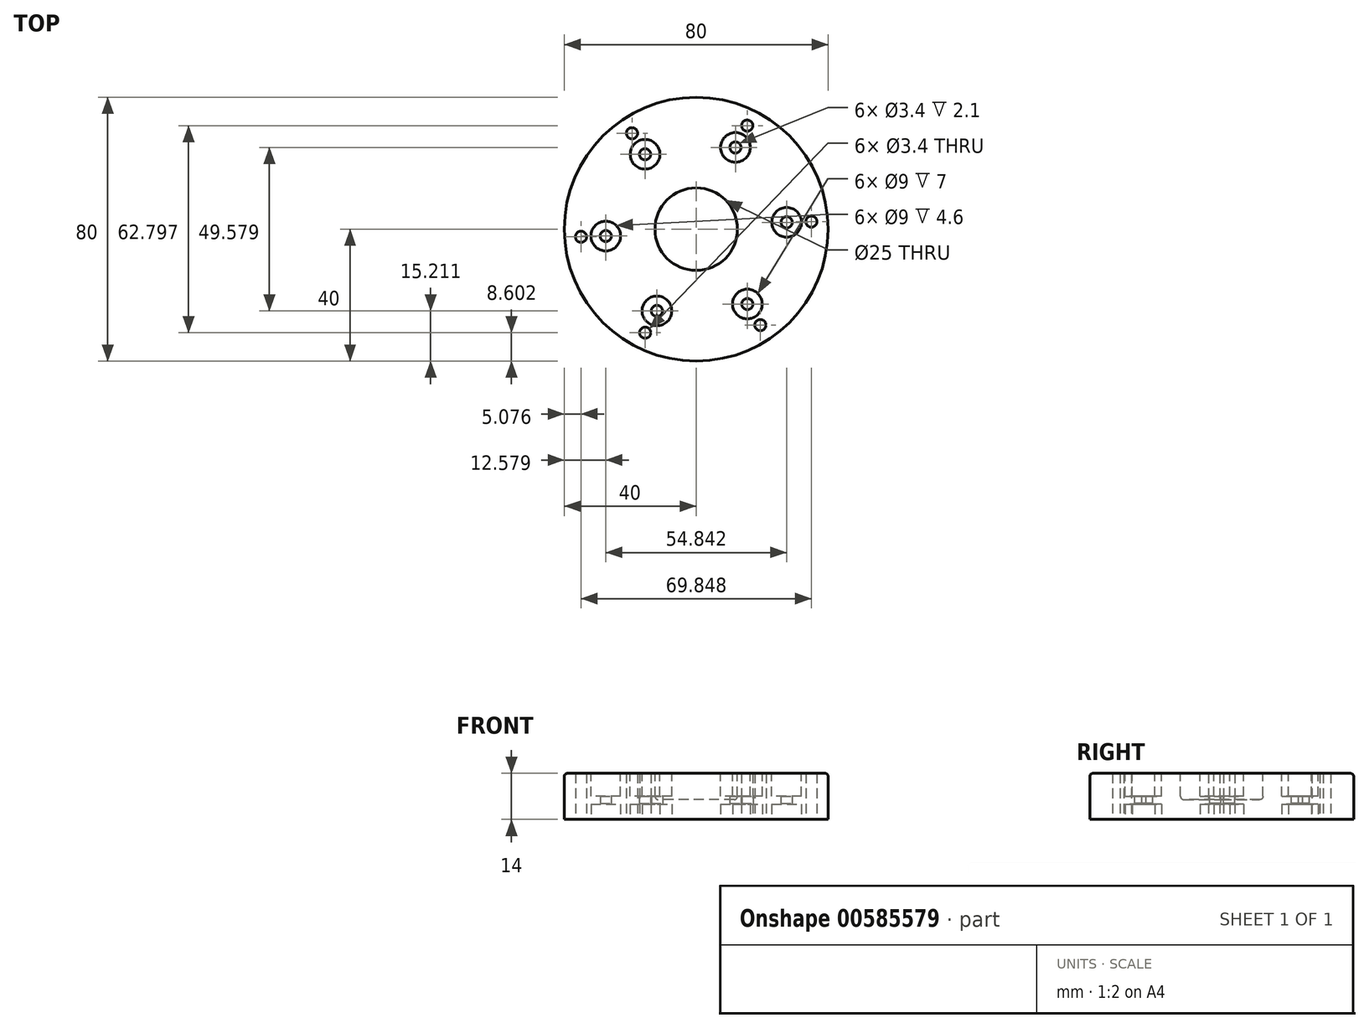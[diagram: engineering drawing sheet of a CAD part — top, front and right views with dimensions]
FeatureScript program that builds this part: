
annotation { "Feature Type Name" : "Feature", "Feature Type Description" : "" }
export const myFeature = defineFeature(function(context is Context, id is Id, definition is map)
    precondition{}
    {
        {
            var Q0;
            Q0=qCreatedBy(makeId("Top.planeOp"),FACE);
            var sketch = newSketch(context, id + "F0", { "sketchPlane" : qUnion([Q0])});
            skCircle(sketch, "E0", {"center": v(0, 0) * mm, "radius": 40 * mm});
            skCircle(sketch, "E1", {"center": v(-19.46, 29.1) * mm, "radius": 1.7 * mm});
            skCircle(sketch, "E2.1.0", {"center": v(15.46, 31.4) * mm, "radius": 1.7 * mm});
            skCircle(sketch, "E2.2.0", {"center": v(34.92, 2.3) * mm, "radius": 1.7 * mm});
            skCircle(sketch, "E2.3.0", {"center": v(19.46, -29.1) * mm, "radius": 1.7 * mm});
            skCircle(sketch, "E2.4.0", {"center": v(-15.46, -31.4) * mm, "radius": 1.7 * mm});
            skCircle(sketch, "E2.5.0", {"center": v(-34.92, -2.3) * mm, "radius": 1.7 * mm});
            skLineSegment(sketch, "E2.anchor1", {"start": v(0, 0) * mm, "end": v(-19.46, 29.1) * mm, "construction": true});
            skLineSegment(sketch, "E2.anchor2", {"start": v(0, 0) * mm, "end": v(-34.92, -2.3) * mm, "construction": true});
            skCircle(sketch, "E3", {"center": v(11.9, 24.79) * mm, "radius": 1.7 * mm});
            skCircle(sketch, "E4.1.0", {"center": v(-15.52, 22.7) * mm, "radius": 1.7 * mm});
            skCircle(sketch, "E4.2.0", {"center": v(-27.42, -2.08) * mm, "radius": 1.7 * mm});
            skCircle(sketch, "E4.3.0", {"center": v(-11.9, -24.79) * mm, "radius": 1.7 * mm});
            skCircle(sketch, "E4.4.0", {"center": v(15.52, -22.7) * mm, "radius": 1.7 * mm});
            skCircle(sketch, "E4.5.0", {"center": v(27.42, 2.08) * mm, "radius": 1.7 * mm});
            skSolve(sketch);
        }
        {
            var Q0;
            Q0=makeQuery(id+"F0.imprint","IMPRINT",FACE,{"disambiguationData":[TD([[makeQuery(id+"F0.imprint","IMPRINT",EDGE,{"derivedFrom":sQuery(id+"F0.wireOp",EDGE,"E1")}),-1.0]])]});
            extrude(context, id + "F1", {"entities" : qUnion([Q0]), "depth" : 14 * mm, "offsetDistance" : 25 * mm});
        }
        {
            var Q0;
            Q0=makeQuery(id+"F1.opExtrude","CAP_FACE",FACE,{"disambiguationData":[OSD([sQuery(id+"F0.wireOp",EDGE,"E1"),sQuery(id+"F0.wireOp",EDGE,"E2.1.0"),sQuery(id+"F0.wireOp",EDGE,"E2.2.0"),sQuery(id+"F0.wireOp",EDGE,"E2.3.0"),sQuery(id+"F0.wireOp",EDGE,"E2.4.0"),sQuery(id+"F0.wireOp",EDGE,"E2.5.0"),sQuery(id+"F0.wireOp",EDGE,"E0"),sQuery(id+"F0.wireOp",EDGE,"E3"),sQuery(id+"F0.wireOp",EDGE,"E4.1.0"),sQuery(id+"F0.wireOp",EDGE,"E4.2.0"),sQuery(id+"F0.wireOp",EDGE,"E4.3.0"),sQuery(id+"F0.wireOp",EDGE,"E4.4.0"),sQuery(id+"F0.wireOp",EDGE,"E4.5.0")])],"isStart":false});
            var sketch = newSketch(context, id + "F2", { "sketchPlane" : qUnion([Q0])});
            skCircle(sketch, "E5.0", {"center": v(-11.9, -24.79) * mm, "radius": 1.7 * mm});
            skCircle(sketch, "E6.0", {"center": v(-27.42, -2.08) * mm, "radius": 1.7 * mm});
            skCircle(sketch, "E7.0", {"center": v(-15.52, 22.7) * mm, "radius": 1.7 * mm});
            skCircle(sketch, "E8.0", {"center": v(11.9, 24.79) * mm, "radius": 1.7 * mm});
            skCircle(sketch, "E9.0", {"center": v(15.52, -22.7) * mm, "radius": 1.7 * mm});
            skCircle(sketch, "E10.0", {"center": v(27.42, 2.08) * mm, "radius": 1.7 * mm});
            skCircle(sketch, "E11", {"center": v(-15.52, 22.7) * mm, "radius": 4.5 * mm});
            skCircle(sketch, "E12.1.0", {"center": v(-27.42, -2.08) * mm, "radius": 4.5 * mm});
            skCircle(sketch, "E12.2.0", {"center": v(-11.9, -24.79) * mm, "radius": 4.5 * mm});
            skCircle(sketch, "E12.3.0", {"center": v(15.52, -22.7) * mm, "radius": 4.5 * mm});
            skCircle(sketch, "E12.4.0", {"center": v(27.42, 2.08) * mm, "radius": 4.5 * mm});
            skCircle(sketch, "E12.5.0", {"center": v(11.9, 24.79) * mm, "radius": 4.5 * mm});
            skPoint(sketch, "E12.center", {"position": v(0, 0) * mm});
            skSolve(sketch);
        }
        {
            var Q0;
            Q0 = qSketchRegion(id + "F2", true);
            extrude(context, id + "F3", {"entities" : qUnion([Q0]), "operationType" : NewBodyOperationType.REMOVE, "oppositeDirection" : true, "depth" : 7 * mm, "offsetDistance" : 25 * mm});
        }
        {
            var Q0;
            Q0=makeQuery(id+"F1.opExtrude","CAP_FACE",FACE,{"disambiguationData":[OSD([sQuery(id+"F0.wireOp",EDGE,"E1"),sQuery(id+"F0.wireOp",EDGE,"E2.1.0"),sQuery(id+"F0.wireOp",EDGE,"E2.2.0"),sQuery(id+"F0.wireOp",EDGE,"E2.3.0"),sQuery(id+"F0.wireOp",EDGE,"E2.4.0"),sQuery(id+"F0.wireOp",EDGE,"E2.5.0"),sQuery(id+"F0.wireOp",EDGE,"E0"),sQuery(id+"F0.wireOp",EDGE,"E3"),sQuery(id+"F0.wireOp",EDGE,"E4.1.0"),sQuery(id+"F0.wireOp",EDGE,"E4.2.0"),sQuery(id+"F0.wireOp",EDGE,"E4.3.0"),sQuery(id+"F0.wireOp",EDGE,"E4.4.0"),sQuery(id+"F0.wireOp",EDGE,"E4.5.0")])],"isStart":true});
            var sketch = newSketch(context, id + "F4", { "sketchPlane" : qUnion([Q0])});
            skCircle(sketch, "E13.0", {"center": v(27.42, -2.08) * mm, "radius": 1.7 * mm});
            skCircle(sketch, "E14", {"center": v(27.42, -2.08) * mm, "radius": 4.5 * mm});
            skCircle(sketch, "E15.1.0", {"center": v(15.52, 22.7) * mm, "radius": 4.5 * mm});
            skCircle(sketch, "E15.2.0", {"center": v(-11.9, 24.79) * mm, "radius": 4.5 * mm});
            skCircle(sketch, "E15.3.0", {"center": v(-27.42, 2.08) * mm, "radius": 4.5 * mm});
            skCircle(sketch, "E15.4.0", {"center": v(-15.52, -22.7) * mm, "radius": 4.5 * mm});
            skCircle(sketch, "E15.5.0", {"center": v(11.9, -24.79) * mm, "radius": 4.5 * mm});
            skPoint(sketch, "E15.center", {"position": v(0, 0) * mm});
            skSolve(sketch);
        }
        {
            var Q0;
            Q0=makeQuery(id+"F4.imprint","IMPRINT",FACE,{"disambiguationData":[TD([[makeQuery(id+"F4.imprint","IMPRINT",EDGE,{"derivedFrom":sQuery(id+"F4.wireOp",EDGE,"E13.0")}),1.0]])]});
            var Q1;
            Q1=makeQuery(id+"F4.imprint","IMPRINT",FACE,{"disambiguationData":[TD([[makeQuery(id+"F4.imprint","IMPRINT",EDGE,{"derivedFrom":sQuery(id+"F4.wireOp",EDGE,"E15.5.0")}),1.0]])]});
            var Q2;
            Q2=makeQuery(id+"F4.imprint","IMPRINT",FACE,{"disambiguationData":[TD([[makeQuery(id+"F4.imprint","IMPRINT",EDGE,{"derivedFrom":sQuery(id+"F4.wireOp",EDGE,"E15.4.0")}),1.0]])]});
            var Q3;
            Q3=makeQuery(id+"F4.imprint","IMPRINT",FACE,{"disambiguationData":[TD([[makeQuery(id+"F4.imprint","IMPRINT",EDGE,{"derivedFrom":sQuery(id+"F4.wireOp",EDGE,"E15.3.0")}),1.0]])]});
            var Q4;
            Q4=makeQuery(id+"F4.imprint","IMPRINT",FACE,{"disambiguationData":[TD([[makeQuery(id+"F4.imprint","IMPRINT",EDGE,{"derivedFrom":sQuery(id+"F4.wireOp",EDGE,"E15.2.0")}),1.0]])]});
            var Q5;
            Q5=makeQuery(id+"F4.imprint","IMPRINT",FACE,{"disambiguationData":[TD([[makeQuery(id+"F4.imprint","IMPRINT",EDGE,{"derivedFrom":sQuery(id+"F4.wireOp",EDGE,"E15.1.0")}),1.0]])]});
            extrude(context, id + "F5", {"entities" : qUnion([Q0, Q1, Q2, Q3, Q4, Q5]), "operationType" : NewBodyOperationType.REMOVE, "oppositeDirection" : true, "depth" : 4.6 * mm, "offsetDistance" : 25 * mm});
        }
        {
            var Q0;
            Q0=makeQuery(id+"F1.opExtrude","CAP_FACE",FACE,{"disambiguationData":[OSD([sQuery(id+"F0.wireOp",EDGE,"E1"),sQuery(id+"F0.wireOp",EDGE,"E2.1.0"),sQuery(id+"F0.wireOp",EDGE,"E2.2.0"),sQuery(id+"F0.wireOp",EDGE,"E2.3.0"),sQuery(id+"F0.wireOp",EDGE,"E2.4.0"),sQuery(id+"F0.wireOp",EDGE,"E2.5.0"),sQuery(id+"F0.wireOp",EDGE,"E0"),sQuery(id+"F0.wireOp",EDGE,"E3"),sQuery(id+"F0.wireOp",EDGE,"E4.1.0"),sQuery(id+"F0.wireOp",EDGE,"E4.2.0"),sQuery(id+"F0.wireOp",EDGE,"E4.3.0"),sQuery(id+"F0.wireOp",EDGE,"E4.4.0"),sQuery(id+"F0.wireOp",EDGE,"E4.5.0")])],"isStart":false});
            var sketch = newSketch(context, id + "F6", { "sketchPlane" : qUnion([Q0])});
            skCircle(sketch, "E16", {"center": v(0, 0) * mm, "radius": 12.5 * mm});
            skSolve(sketch);
        }
        {
            var Q0;
            Q0=makeQuery(id+"F6.imprint","IMPRINT",FACE,{"disambiguationData":[TD([[makeQuery(id+"F6.imprint","IMPRINT",EDGE,{"derivedFrom":sQuery(id+"F6.wireOp",EDGE,"E16")}),1.0]])]});
            extrude(context, id + "F7", {"entities" : qUnion([Q0]), "operationType" : NewBodyOperationType.REMOVE, "oppositeDirection" : true, "depth" : 8 * mm, "offsetDistance" : 25 * mm});
        }
        {
            var Q0;
            Q0=makeQuery(id+"F7.boolean.opBoolean","COPY",EDGE,{"derivedFrom":makeQuery(id+"F7.opExtrude","CAP_EDGE",EDGE,{"disambiguationData":[OSD([sQuery(id+"F6.wireOp",EDGE,"E16")])],"isStart":false})});
            var Q1;
            Q1=makeQuery(id+"F7.boolean.opBoolean","COPY",EDGE,{"derivedFrom":makeQuery(id+"F7.opExtrude","CAP_EDGE",EDGE,{"disambiguationData":[OSD([sQuery(id+"F6.wireOp",EDGE,"E16")])],"isStart":true})});
            var Q2;
            Q2=makeQuery(id+"F1.opExtrude","CAP_EDGE",EDGE,{"disambiguationData":[OSD([sQuery(id+"F0.wireOp",EDGE,"E0")])],"isStart":false});
            fillet(context, id + "F8", {"entities" : qUnion([Q0, Q1, Q2]), "radius" : 1 * mm, "tangentPropagation" : true, "allowEdgeOverflow" : false});
        }
        {
            var Q0;
            Q0=makeQuery(id+"F5.boolean.opBoolean","COPY",FACE,{"derivedFrom":makeQuery(id+"F5.opExtrude","CAP_FACE",FACE,{"disambiguationData":[OSD([sQuery(id+"F0.wireOp",EDGE,"E4.1.0"),sQuery(id+"F4.wireOp",EDGE,"E15.4.0")])],"isStart":false})});
            cPlane(context, id + "F9", {"entities" : qUnion([Q0]), "cplaneType" : CPlaneType.OFFSET, "offset" : 0 * mm, "width" : 150 * mm, "height" : 150 * mm});
        }
        {
            var Q0;
            Q0=qCreatedBy(id+"F9.planeOp",FACE);
            var sketch = newSketch(context, id + "F10", { "sketchPlane" : qUnion([Q0])});
            skCircle(sketch, "E17", {"center": v(0, 0) * mm, "radius": 32.16 * mm});
            skSolve(sketch);
        }
        {
            var Q0;
            Q0 = qSketchRegion(id + "F10", true);
            extrude(context, id + "F11", {"entities" : qUnion([Q0]), "operationType" : NewBodyOperationType.ADD, "oppositeDirection" : true, "depth" : 0.3 * mm, "offsetDistance" : 25 * mm});
        }
    });
